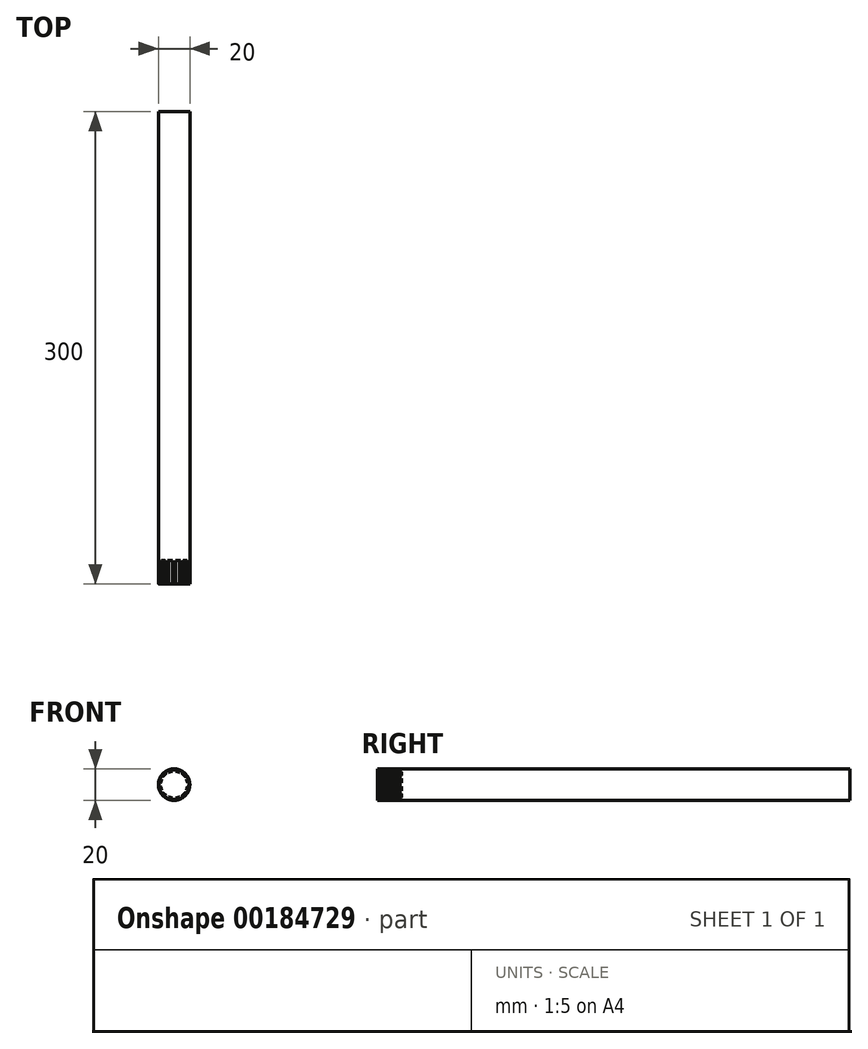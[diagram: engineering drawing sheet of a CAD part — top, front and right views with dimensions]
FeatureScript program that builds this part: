
annotation { "Feature Type Name" : "Feature", "Feature Type Description" : "" }
export const myFeature = defineFeature(function(context is Context, id is Id, definition is map)
    precondition{}
    {
        {
            var Q0;
            Q0=qCreatedBy(makeId("Front.planeOp"),FACE);
            var sketch = newSketch(context, id + "F0", { "sketchPlane" : qUnion([Q0])});
            skCircle(sketch, "E0", {"center": v(0, 0) * mm, "radius": 10 * mm});
            skSolve(sketch);
        }
        {
            var Q0;
            Q0 = qSketchRegion(id + "F0", true);
            extrude(context, id + "F1", {"entities" : qUnion([Q0]), "endBound" : BoundingType.SYMMETRIC, "depth" : 300 * mm});
        }
        {
            var Q0;
            Q0=makeQuery(id+"F1.opExtrude","CAP_FACE",FACE,{"disambiguationData":[OSD([sQuery(id+"F0.wireOp",EDGE,"E0")])],"isStart":false});
            var sketch = newSketch(context, id + "F2", { "sketchPlane" : qUnion([Q0])});
            skCircle(sketch, "E1", {"center": v(0, 0) * mm, "radius": 10.03 * mm});
            skLineSegment(sketch, "E2.0", {"start": v(1, 8.47) * mm, "end": v(1, 10) * mm});
            skLineSegment(sketch, "E3.0", {"start": v(-1, 8.47) * mm, "end": v(-1, 10) * mm});
            skCircle(sketch, "E4.0", {"center": v(0, 0) * mm, "radius": 8.53 * mm});
            skLineSegment(sketch, "E5.1.0", {"start": v(-5.1, 6.83) * mm, "end": v(-5.87, 8.16) * mm});
            skLineSegment(sketch, "E5.1.1", {"start": v(-3.37, 7.83) * mm, "end": v(-4.13, 9.16) * mm});
            skLineSegment(sketch, "E5.2.0", {"start": v(-7.83, 3.37) * mm, "end": v(-9.16, 4.13) * mm});
            skLineSegment(sketch, "E5.2.1", {"start": v(-6.83, 5.1) * mm, "end": v(-8.16, 5.87) * mm});
            skLineSegment(sketch, "E6.1.3.0", {"start": v(-8.47, -1) * mm, "end": v(-10, -1) * mm});
            skLineSegment(sketch, "E6.3.3.0", {"start": v(-8.47, 1) * mm, "end": v(-10, 1) * mm});
            skLineSegment(sketch, "E6.1.4.0", {"start": v(-6.83, -5.1) * mm, "end": v(-8.16, -5.87) * mm});
            skLineSegment(sketch, "E6.3.4.0", {"start": v(-7.83, -3.37) * mm, "end": v(-9.16, -4.13) * mm});
            skLineSegment(sketch, "E6.1.5.0", {"start": v(-3.37, -7.83) * mm, "end": v(-4.13, -9.16) * mm});
            skLineSegment(sketch, "E6.3.5.0", {"start": v(-5.1, -6.83) * mm, "end": v(-5.87, -8.16) * mm});
            skLineSegment(sketch, "E7.1.6.0", {"start": v(1, -8.47) * mm, "end": v(1, -10) * mm});
            skLineSegment(sketch, "E7.3.6.0", {"start": v(-1, -8.47) * mm, "end": v(-1, -10) * mm});
            skLineSegment(sketch, "E7.1.7.0", {"start": v(5.1, -6.83) * mm, "end": v(5.87, -8.16) * mm});
            skLineSegment(sketch, "E7.3.7.0", {"start": v(3.37, -7.83) * mm, "end": v(4.13, -9.16) * mm});
            skLineSegment(sketch, "E7.1.8.0", {"start": v(7.83, -3.37) * mm, "end": v(9.16, -4.13) * mm});
            skLineSegment(sketch, "E7.3.8.0", {"start": v(6.83, -5.1) * mm, "end": v(8.16, -5.87) * mm});
            skLineSegment(sketch, "E7.1.9.0", {"start": v(8.47, 1) * mm, "end": v(10, 1) * mm});
            skLineSegment(sketch, "E7.3.9.0", {"start": v(8.47, -1) * mm, "end": v(10, -1) * mm});
            skLineSegment(sketch, "E7.1.10.0", {"start": v(6.83, 5.1) * mm, "end": v(8.16, 5.87) * mm});
            skLineSegment(sketch, "E7.3.10.0", {"start": v(7.83, 3.37) * mm, "end": v(9.16, 4.13) * mm});
            skLineSegment(sketch, "E7.1.11.0", {"start": v(3.37, 7.83) * mm, "end": v(4.13, 9.16) * mm});
            skLineSegment(sketch, "E7.3.11.0", {"start": v(5.1, 6.83) * mm, "end": v(5.87, 8.16) * mm});
            skSolve(sketch);
        }
        {
            var Q0;
            {var subQ0=sQuery(id+"F2.wireOp",EDGE,"E4.0");var subQ1=sQuery(id+"F2.wireOp",EDGE,"E3.0");var subQ2=makeQuery(id+"F2.imprint","INTERSECT",VERTEX,{"derivedFrom":[subQ1,subQ0]});Q0=makeQuery(id+"F2.imprint","IMPRINT",FACE,{"disambiguationData":[TD([[makeQuery(id+"F2.imprint","IMPRINT",EDGE,{"disambiguationData":[TD([[subQ2,-1.0]])],"derivedFrom":subQ1}),1.0]])]});}
            var Q1;
            {var subQ0=sQuery(id+"F2.wireOp",EDGE,"E4.0");var subQ1=sQuery(id+"F2.wireOp",EDGE,"E2.0");var subQ2=makeQuery(id+"F2.imprint","INTERSECT",VERTEX,{"derivedFrom":[subQ1,subQ0]});Q1=makeQuery(id+"F2.imprint","IMPRINT",FACE,{"disambiguationData":[TD([[makeQuery(id+"F2.imprint","IMPRINT",EDGE,{"disambiguationData":[TD([[subQ2,-1.0]])],"derivedFrom":subQ1}),-1.0]])]});}
            var Q2;
            {var subQ0=sQuery(id+"F2.wireOp",EDGE,"E7.1.10.0");var subQ1=sQuery(id+"F2.wireOp",EDGE,"E4.0");var subQ2=makeQuery(id+"F2.imprint","INTERSECT",VERTEX,{"derivedFrom":[subQ1,subQ0]});Q2=makeQuery(id+"F2.imprint","IMPRINT",FACE,{"disambiguationData":[TD([[makeQuery(id+"F2.imprint","IMPRINT",EDGE,{"disambiguationData":[TD([[subQ2,-1.0]])],"derivedFrom":subQ1}),-1.0]])]});}
            var Q3;
            {var subQ0=sQuery(id+"F2.wireOp",EDGE,"E7.1.9.0");var subQ1=sQuery(id+"F2.wireOp",EDGE,"E4.0");var subQ2=makeQuery(id+"F2.imprint","INTERSECT",VERTEX,{"derivedFrom":[subQ1,subQ0]});Q3=makeQuery(id+"F2.imprint","IMPRINT",FACE,{"disambiguationData":[TD([[makeQuery(id+"F2.imprint","IMPRINT",EDGE,{"disambiguationData":[TD([[subQ2,-1.0]])],"derivedFrom":subQ1}),-1.0]])]});}
            var Q4;
            {var subQ0=sQuery(id+"F2.wireOp",EDGE,"E7.1.8.0");var subQ1=sQuery(id+"F2.wireOp",EDGE,"E4.0");var subQ2=makeQuery(id+"F2.imprint","INTERSECT",VERTEX,{"derivedFrom":[subQ1,subQ0]});Q4=makeQuery(id+"F2.imprint","IMPRINT",FACE,{"disambiguationData":[TD([[makeQuery(id+"F2.imprint","IMPRINT",EDGE,{"disambiguationData":[TD([[subQ2,-1.0]])],"derivedFrom":subQ1}),-1.0]])]});}
            var Q5;
            {var subQ0=sQuery(id+"F2.wireOp",EDGE,"E7.1.7.0");var subQ1=sQuery(id+"F2.wireOp",EDGE,"E4.0");var subQ2=makeQuery(id+"F2.imprint","INTERSECT",VERTEX,{"derivedFrom":[subQ1,subQ0]});Q5=makeQuery(id+"F2.imprint","IMPRINT",FACE,{"disambiguationData":[TD([[makeQuery(id+"F2.imprint","IMPRINT",EDGE,{"disambiguationData":[TD([[subQ2,-1.0]])],"derivedFrom":subQ1}),-1.0]])]});}
            var Q6;
            {var subQ0=sQuery(id+"F2.wireOp",EDGE,"E7.1.6.0");var subQ1=sQuery(id+"F2.wireOp",EDGE,"E4.0");var subQ2=makeQuery(id+"F2.imprint","INTERSECT",VERTEX,{"derivedFrom":[subQ1,subQ0]});Q6=makeQuery(id+"F2.imprint","IMPRINT",FACE,{"disambiguationData":[TD([[makeQuery(id+"F2.imprint","IMPRINT",EDGE,{"disambiguationData":[TD([[subQ2,-1.0]])],"derivedFrom":subQ1}),-1.0]])]});}
            var Q7;
            {var subQ0=sQuery(id+"F2.wireOp",EDGE,"E6.1.5.0");var subQ1=sQuery(id+"F2.wireOp",EDGE,"E4.0");var subQ2=makeQuery(id+"F2.imprint","INTERSECT",VERTEX,{"derivedFrom":[subQ1,subQ0]});Q7=makeQuery(id+"F2.imprint","IMPRINT",FACE,{"disambiguationData":[TD([[makeQuery(id+"F2.imprint","IMPRINT",EDGE,{"disambiguationData":[TD([[subQ2,-1.0]])],"derivedFrom":subQ1}),-1.0]])]});}
            var Q8;
            {var subQ0=sQuery(id+"F2.wireOp",EDGE,"E6.1.4.0");var subQ1=sQuery(id+"F2.wireOp",EDGE,"E4.0");var subQ2=makeQuery(id+"F2.imprint","INTERSECT",VERTEX,{"derivedFrom":[subQ1,subQ0]});Q8=makeQuery(id+"F2.imprint","IMPRINT",FACE,{"disambiguationData":[TD([[makeQuery(id+"F2.imprint","IMPRINT",EDGE,{"disambiguationData":[TD([[subQ2,-1.0]])],"derivedFrom":subQ1}),-1.0]])]});}
            var Q9;
            {var subQ0=sQuery(id+"F2.wireOp",EDGE,"E6.1.3.0");var subQ1=sQuery(id+"F2.wireOp",EDGE,"E4.0");var subQ2=makeQuery(id+"F2.imprint","INTERSECT",VERTEX,{"derivedFrom":[subQ1,subQ0]});Q9=makeQuery(id+"F2.imprint","IMPRINT",FACE,{"disambiguationData":[TD([[makeQuery(id+"F2.imprint","IMPRINT",EDGE,{"disambiguationData":[TD([[subQ2,-1.0]])],"derivedFrom":subQ1}),-1.0]])]});}
            var Q10;
            {var subQ0=sQuery(id+"F2.wireOp",EDGE,"E5.2.0");var subQ1=sQuery(id+"F2.wireOp",EDGE,"E4.0");var subQ2=makeQuery(id+"F2.imprint","INTERSECT",VERTEX,{"derivedFrom":[subQ1,subQ0]});Q10=makeQuery(id+"F2.imprint","IMPRINT",FACE,{"disambiguationData":[TD([[makeQuery(id+"F2.imprint","IMPRINT",EDGE,{"disambiguationData":[TD([[subQ2,-1.0]])],"derivedFrom":subQ1}),-1.0]])]});}
            var Q11;
            {var subQ0=sQuery(id+"F2.wireOp",EDGE,"E5.1.0");var subQ1=sQuery(id+"F2.wireOp",EDGE,"E4.0");var subQ2=makeQuery(id+"F2.imprint","INTERSECT",VERTEX,{"derivedFrom":[subQ1,subQ0]});Q11=makeQuery(id+"F2.imprint","IMPRINT",FACE,{"disambiguationData":[TD([[makeQuery(id+"F2.imprint","IMPRINT",EDGE,{"disambiguationData":[TD([[subQ2,-1.0]])],"derivedFrom":subQ1}),-1.0]])]});}
            extrude(context, id + "F3", {"entities" : qUnion([Q0, Q1, Q2, Q3, Q4, Q5, Q6, Q7, Q8, Q9, Q10, Q11]), "operationType" : NewBodyOperationType.REMOVE, "oppositeDirection" : true, "depth" : 15 * mm});
        }
    });
